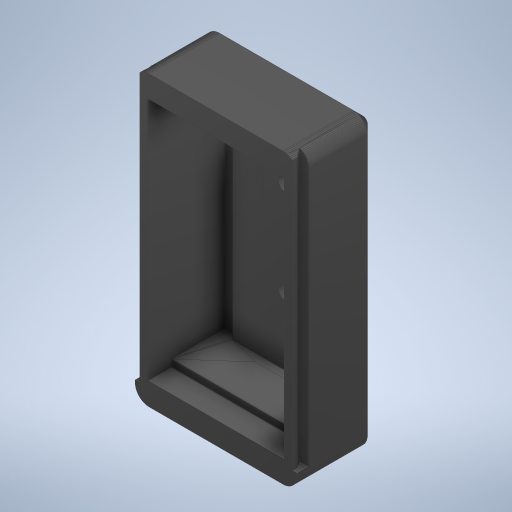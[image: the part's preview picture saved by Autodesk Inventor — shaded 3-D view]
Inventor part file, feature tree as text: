
AUTODESK INVENTOR PART (.ipt)
format: ipt  version: 2024.3 (Build 283343000, 343)  size: 1,974,784 bytes
history: native  units: mm
features: other x5, extrude x4, sketch x4
ambient origin geometry x8: Origin, YZ Plane, XZ Plane, XY Plane, X Axis, Y Axis, Z Axis, Center Point
bodies: Body1 (feature_tree), Body2 (feature_tree)
feature tree (13):
  other  "Sólido1"
  other  "ESP32_DEVKIT_V1_Case"
  other  "Coser superficie1"
  extrude  "Extrusión1"  Depth=11.479638mm
  extrude  "Extrusión2"  Depth=10.0mm TaperAngle=0.0deg
  extrude  "Extrusión3"  Depth=0.6mm
  extrude  "Extrusión4"  Depth=13.0mm
  sketch  "Boceto1"  dims[d0=11.479638mm d1=40.440399mm]
  sketch  "Boceto2"  dims[d2=9.377155mm d3=10.0mm d4=0.0mm]
  sketch  "Boceto3"  dims[d5=13.0mm d6=0.6mm]
  sketch  "Boceto4"  dims[d7=0.0mm d8=13.0mm d9=27.0mm d10=2.0mm d11=0.0mm d12=0.0mm d13=4.75mm d14=12.0mm d15=0.0mm d16=12.0mm d17=0.0mm]
  other  "Compuesto1"
  other  "Sup1"
